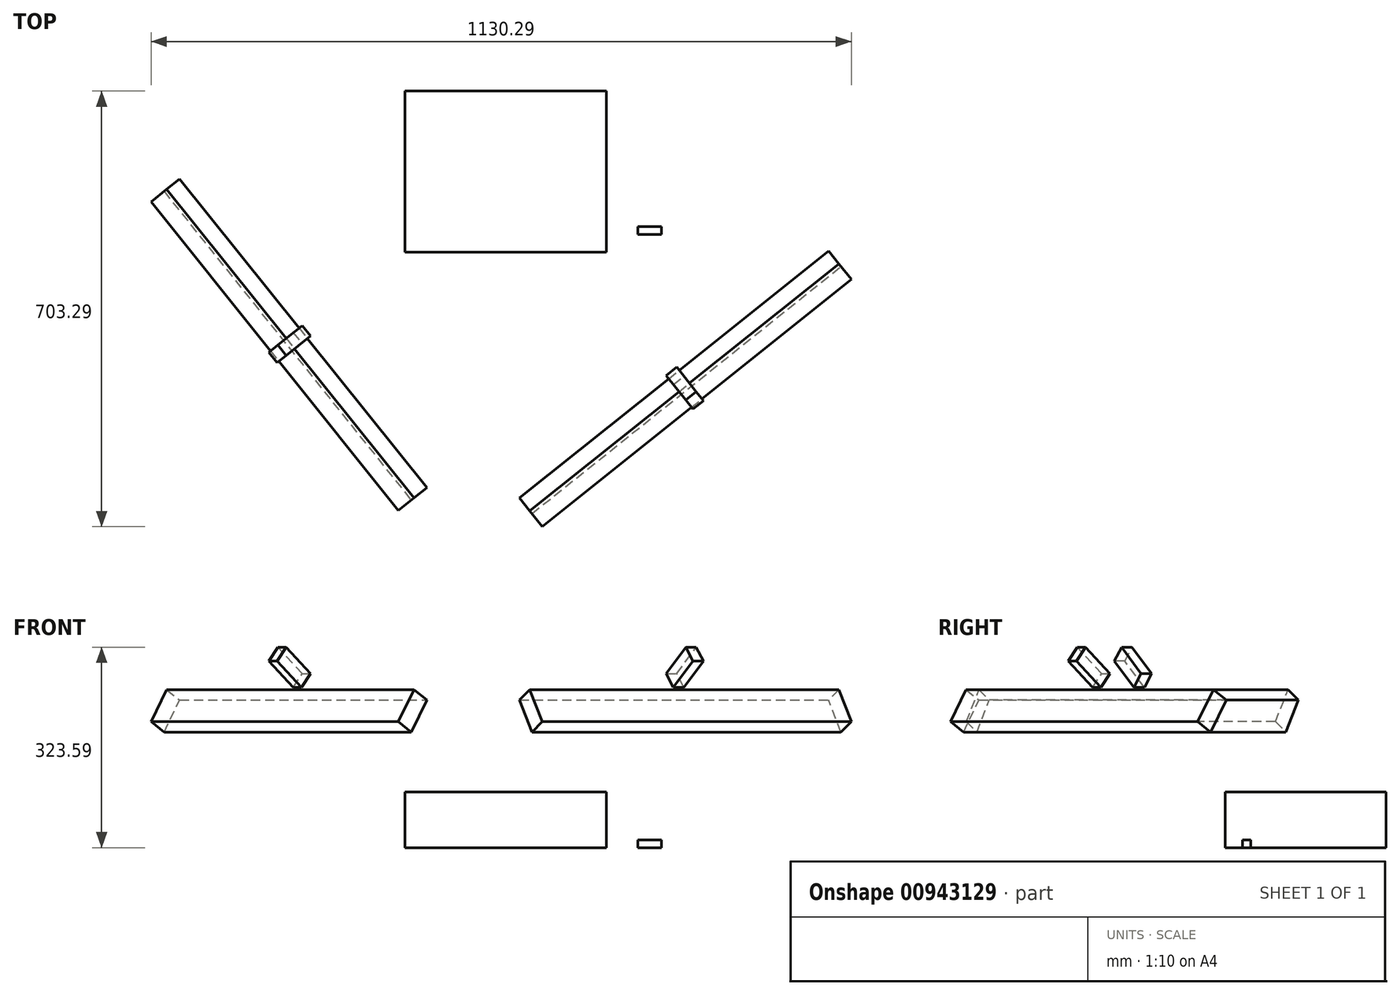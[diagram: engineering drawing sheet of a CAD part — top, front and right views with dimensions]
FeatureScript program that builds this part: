
annotation { "Feature Type Name" : "Feature", "Feature Type Description" : "" }
export const myFeature = defineFeature(function(context is Context, id is Id, definition is map)
    precondition{}
    {
        {
            var Q0;
            Q0=qCreatedBy(makeId("Top.planeOp"),FACE);
            var sketch = newSketch(context, id + "F0", { "sketchPlane" : qUnion([Q0])});
            skLineSegment(sketch, "E0.bottom", {"start": v(-162.5, -130) * mm, "end": v(162.5, -130) * mm});
            skLineSegment(sketch, "E0.top", {"start": v(-162.5, 130) * mm, "end": v(162.5, 130) * mm});
            skLineSegment(sketch, "E0.left", {"start": v(-162.5, -130) * mm, "end": v(-162.5, 130) * mm});
            skLineSegment(sketch, "E0.right", {"start": v(162.5, -130) * mm, "end": v(162.5, 130) * mm});
            skSolve(sketch);
        }
        {
            var Q0;
            Q0=makeQuery(id+"F0.imprint","IMPRINT",FACE,{"disambiguationData":[TD([[makeQuery(id+"F0.imprint","IMPRINT",EDGE,{"derivedFrom":sQuery(id+"F0.wireOp",EDGE,"E0.bottom")}),1.0]])]});
            extrude(context, id + "F1", {"entities" : qUnion([Q0]), "depth" : 90 * mm, "offsetDistance" : 25.4 * mm});
        }
        {
            var Q0;
            Q0=makeQuery(id+"F1.opExtrude","CAP_FACE",FACE,{"disambiguationData":[OSD([sQuery(id+"F0.wireOp",EDGE,"E0.bottom"),sQuery(id+"F0.wireOp",EDGE,"E0.top"),sQuery(id+"F0.wireOp",EDGE,"E0.left"),sQuery(id+"F0.wireOp",EDGE,"E0.right")])],"isStart":true});
            var sketch = newSketch(context, id + "F2", { "sketchPlane" : qUnion([Q0])});
            skLineSegment(sketch, "E1", {"start": v(162.5, 130) * mm, "end": v(162.5, 130) * mm});
            skLineSegment(sketch, "E2", {"start": v(162.5, 130) * mm, "end": v(-162.5, -130) * mm});
            skPoint(sketch, "E3", {"position": v(0, 0) * mm});
            skLineSegment(sketch, "E4", {"start": v(162.5, 130) * mm, "end": v(-326.88, 261.5) * mm});
            skLineSegment(sketch, "E5", {"start": v(-326.88, 261.5) * mm, "end": v(-162.5, -130) * mm});
            skLineSegment(sketch, "E6", {"start": v(-326.88, 261.5) * mm, "end": v(0, 0) * mm});
            skLineSegment(sketch, "E7", {"start": v(130, 162.5) * mm, "end": v(-130, -162.5) * mm});
            skSolve(sketch);
        }
        {
            var Q0;
            Q0=sQuery(id+"F2.wireOp",EDGE,"E6");
            cPlane(context, id + "F3", {"entities" : qUnion([Q0]), "cplaneType" : CPlaneType.LINE_ANGLE, "offset" : 25.4 * mm, "angle" : 0 * degree, "width" : 152.4 * mm, "height" : 152.4 * mm});
        }
        {
            var Q0;
            Q0=qCreatedBy(id+"F3.planeOp",FACE);
            var sketch = newSketch(context, id + "F4", { "sketchPlane" : qUnion([Q0])});
            skPoint(sketch, "E8", {"position": v(420.84, 270) * mm});
            skSolve(sketch);
        }
        {
            var Q0;
            Q0=qCreatedBy(id+"F3.planeOp",FACE);
            var sketch = newSketch(context, id + "F5", { "sketchPlane" : qUnion([Q0])});
            skLineSegment(sketch, "E9.bottom", {"start": v(430.18, 258.86) * mm, "end": v(480.77, 301.31) * mm});
            skLineSegment(sketch, "E9.top", {"start": v(411.49, 281.14) * mm, "end": v(462.08, 323.6) * mm});
            skLineSegment(sketch, "E9.left", {"start": v(430.18, 258.86) * mm, "end": v(411.49, 281.14) * mm});
            skLineSegment(sketch, "E9.right", {"start": v(480.77, 301.31) * mm, "end": v(462.08, 323.6) * mm});
            skSolve(sketch);
        }
        {
            var Q0;
            Q0=makeQuery(id+"F5.imprint","IMPRINT",FACE,{"disambiguationData":[TD([[makeQuery(id+"F5.imprint","IMPRINT",EDGE,{"derivedFrom":sQuery(id+"F5.wireOp",EDGE,"E9.bottom")}),1.0]])]});
            extrude(context, id + "F6", {"entities" : qUnion([Q0]), "endBound" : BoundingType.SYMMETRIC, "depth" : 21.59 * mm, "offsetDistance" : 25.4 * mm});
        }
        {
            var Q0;
            Q0=qCreatedBy(id+"F3.planeOp",FACE);
            var sketch = newSketch(context, id + "F7", { "sketchPlane" : qUnion([Q0])});
            skLineSegment(sketch, "E10.bottom", {"start": v(477.12, 203.34) * mm, "end": v(450.4, 186.65) * mm});
            skLineSegment(sketch, "E10.top", {"start": v(444.81, 255.03) * mm, "end": v(418.1, 238.34) * mm});
            skLineSegment(sketch, "E10.left", {"start": v(477.12, 203.34) * mm, "end": v(444.81, 255.03) * mm});
            skLineSegment(sketch, "E10.right", {"start": v(450.4, 186.65) * mm, "end": v(418.1, 238.34) * mm});
            skSolve(sketch);
        }
        {
            var Q0;
            Q0=makeQuery(id+"F7.imprint","IMPRINT",FACE,{"disambiguationData":[TD([[makeQuery(id+"F7.imprint","IMPRINT",EDGE,{"derivedFrom":sQuery(id+"F7.wireOp",EDGE,"E10.bottom")}),-1.0]])]});
            extrude(context, id + "F8", {"entities" : qUnion([Q0]), "endBound" : BoundingType.SYMMETRIC, "depth" : 638.8 * mm, "offsetDistance" : 25.4 * mm});
        }
        {
            var Q0;
            Q0=qCreatedBy(id+"F3.planeOp",FACE);
            var sketch = newSketch(context, id + "F9", { "sketchPlane" : qUnion([Q0])});
            skLineSegment(sketch, "E11", {"start": v(-215.47, 93.15) * mm, "end": v(200.21, 93.15) * mm});
            skPoint(sketch, "E12", {"position": v(-7.63, 93.15) * mm});
            skLineSegment(sketch, "E13", {"start": v(-7.63, 93.15) * mm, "end": v(-7.63, 191.28) * mm});
            skLineSegment(sketch, "E14", {"start": v(-7.63, 191.28) * mm, "end": v(200.21, 93.15) * mm});
            skLineSegment(sketch, "E15", {"start": v(-7.63, 191.28) * mm, "end": v(-215.47, 93.15) * mm});
            skSolve(sketch);
        }
        {
            var Q0;
            Q0=makeQuery(id+"F6.opExtrude","SWEPT_BODY",BODY,{"disambiguationData":[OSD([sQuery(id+"F5.wireOp",EDGE,"E9.bottom"),sQuery(id+"F5.wireOp",EDGE,"E9.top"),sQuery(id+"F5.wireOp",EDGE,"E9.left"),sQuery(id+"F5.wireOp",EDGE,"E9.right")])]});
            var Q1;
            Q1=makeQuery(id+"F8.opExtrude","SWEPT_BODY",BODY,{"disambiguationData":[OSD([sQuery(id+"F7.wireOp",EDGE,"E10.bottom"),sQuery(id+"F7.wireOp",EDGE,"E10.top"),sQuery(id+"F7.wireOp",EDGE,"E10.left"),sQuery(id+"F7.wireOp",EDGE,"E10.right")])]});
            var Q2;
            Q2=sQuery(id+"F9.wireOp",EDGE,"E13");
            circularPattern(context, id + "F10", {"entities" : qUnion([Q0, Q1]), "axis" : qUnion([Q2]), "angle" : 90 * degree, "instanceCount" : 2, "equalSpace" : true});
        }
        {
            var Q0;
            Q0=makeQuery(id+"F1.opExtrude","CAP_FACE",FACE,{"disambiguationData":[OSD([sQuery(id+"F0.wireOp",EDGE,"E0.bottom"),sQuery(id+"F0.wireOp",EDGE,"E0.top"),sQuery(id+"F0.wireOp",EDGE,"E0.left"),sQuery(id+"F0.wireOp",EDGE,"E0.right")])],"isStart":true});
            var sketch = newSketch(context, id + "F11", { "sketchPlane" : qUnion([Q0])});
            skLineSegment(sketch, "E16.bottom", {"start": v(-111.13, -95.25) * mm, "end": v(111.12, -95.25) * mm});
            skLineSegment(sketch, "E16.top", {"start": v(-111.13, 95.25) * mm, "end": v(111.12, 95.25) * mm});
            skLineSegment(sketch, "E16.left", {"start": v(-111.13, -95.25) * mm, "end": v(-111.13, 95.25) * mm});
            skLineSegment(sketch, "E16.right", {"start": v(111.12, -95.25) * mm, "end": v(111.12, 95.25) * mm});
            skSolve(sketch);
        }
        {
            var Q0;
            Q0=qCreatedBy(makeId("Front.planeOp"),FACE);
            cPlane(context, id + "F12", {"entities" : qUnion([Q0]), "cplaneType" : CPlaneType.OFFSET, "offset" : 95.25 * mm, "width" : 152.4 * mm, "height" : 152.4 * mm});
        }
        {
            var Q0;
            Q0=qCreatedBy(id+"F12.planeOp",FACE);
            var sketch = newSketch(context, id + "F13", { "sketchPlane" : qUnion([Q0])});
            skLineSegment(sketch, "E17.bottom", {"start": v(213.3, 0) * mm, "end": v(251.4, 0) * mm});
            skLineSegment(sketch, "E17.top", {"start": v(213.3, 12.7) * mm, "end": v(251.4, 12.7) * mm});
            skLineSegment(sketch, "E17.left", {"start": v(213.3, 0) * mm, "end": v(213.3, 12.7) * mm});
            skLineSegment(sketch, "E17.right", {"start": v(251.4, 0) * mm, "end": v(251.4, 12.7) * mm});
            skSolve(sketch);
        }
        {
            var Q0;
            Q0=makeQuery(id+"F13.imprint","IMPRINT",FACE,{"disambiguationData":[TD([[makeQuery(id+"F13.imprint","IMPRINT",EDGE,{"derivedFrom":sQuery(id+"F13.wireOp",EDGE,"E17.bottom")}),1.0]])]});
            extrude(context, id + "F14", {"entities" : qUnion([Q0]), "endBound" : BoundingType.SYMMETRIC, "depth" : 12.7 * mm, "offsetDistance" : 25.4 * mm});
        }
    });
